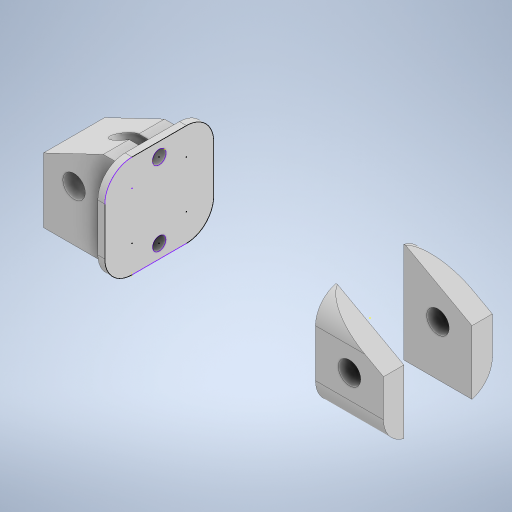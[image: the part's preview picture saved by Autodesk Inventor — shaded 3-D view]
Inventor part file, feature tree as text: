
AUTODESK INVENTOR PART (.ipt)
format: ipt  version: 2024 (Build 280153000, 153)  size: 498,176 bytes
history: native  units: mm
features: sketch x25, extrude x19, chamfer x3, plane x2, split x2, move_body x2, fillet x1, boolean_combine x1
ambient origin geometry x8: Origin, YZ Plane, XZ Plane, XY Plane, X Axis, Y Axis, Z Axis, Center Point
bodies: Solid1 (feature_tree), Solid2 (feature_tree), Solid3 (feature_tree), Solid4 (feature_tree), Solid5 (feature_tree)
feature tree (55):
  extrude  "Extrusion1"  Depth=16.0mm
  sketch  "Sketch2"  dims[d2=15.0mm d3=0.0mm d4=10.0mm]
  extrude  "Extrusion2"  Depth=10.0mm
  chamfer  "Chamfer1"  Distance=21.25mm
  extrude  "Extrusion3"  Depth=10.0mm TaperAngle=0.0deg
  extrude  "Extrusion4"  Depth=11.5mm TaperAngle=0.0deg
  extrude  "Extrusion5"  Depth=1.0mm TaperAngle=0.0deg
  chamfer  "Chamfer2"  Distance=6.0mm Angle=45.0deg
  sketch  "Sketch6"  dims[d14=7.0mm d15=11.5mm d16=0.0mm]
  extrude  "Extrusion6"  Depth=9.0mm
  extrude  "Extrusion7"  Depth=11.5mm TaperAngle=0.0deg
  chamfer  "Chamfer3"  Distance=11.5mm Angle=45.0deg
  sketch  "Sketch9"  dims[d26=3.3mm d27=45.25mm d28=0.0mm d29=11.5mm d30=5.5mm d31=45.0deg]
  extrude  "Extrusion8"  Depth=65.75mm TaperAngle=0.0deg
  extrude  "Extrusion9"  Depth=9.0mm TaperAngle=0.0deg
  extrude  "Extrusion10"  Depth=13.0mm TaperAngle=0.0deg
  sketch  "Sketch13"  dims[d43=24.0mm d44=21.0mm d45=0.0mm]
  extrude  "Extrusion11"  Depth=21.0mm TaperAngle=0.0deg
  extrude  "Extrusion12"  TaperAngle=0.0deg  [1 undecoded]
  extrude  "Extrusion13"  Depth=6.0mm TaperAngle=0.0deg
  plane  "Work Plane1"
  split  "Split1"
  move_body  "Move Body1"
  extrude  "Extrusion14"  Depth=0.5mm TaperAngle=0.0deg
  move_body  "Move Body2"
  fillet  "Fillet1"  Radius=10.0mm
  extrude  "Extrusion15"  Depth=10.0mm TaperAngle=0.0deg
  sketch  "Sketch19"  dims[d71=29.5mm d72=0.0mm d73=13.75mm]
  sketch  "Sketch20"
  extrude  "Extrusion16"  Depth=31.0mm
  extrude  "Extrusion18"  Depth=13.75mm
  extrude  "Extrusion19"  [1 undecoded]
  sketch  "Sketch23"
  sketch  "Sketch24"
  extrude  "Extrusion20"  [1 undecoded]
  plane  "Work Plane2"
  boolean_combine  "Combine1"
  split  "Split2"
  sketch  "Sketch26"
  sketch  "Sketch1"  dims[d0=36.0mm d1=16.0mm]
  sketch  "Sketch3"  dims[d5=10.0mm]
  sketch  "Sketch4"  dims[d6=3.3mm d7=21.25mm d8=0.0mm]
  sketch  "Sketch5"  dims[d9=10.0mm d10=5.5mm d11=45.0deg d12=10.0mm d13=0.0mm]
  sketch  "Sketch7"  dims[d17=3.3mm d18=1.0mm d19=0.0mm d20=6.0mm d21=11.5mm d22=45.0deg]
  sketch  "Sketch8"  dims[d23=15.0mm d24=0.0mm d25=9.0mm]
  sketch  "Sketch10"  dims[d32=2.0mm d33=65.75mm d34=0.0mm]
  sketch  "Sketch11"  dims[d35=0.5mm d36=0.0mm d37=9.0mm d38=0.0mm]
  sketch  "Sketch12"  dims[d39=0.5mm d40=0.0mm d41=13.0mm d42=0.0mm]
  sketch  "Sketch14"  dims[d46=12.25mm d47=-12.0mm d48=0.0mm d49=0.0mm]
  sketch  "Sketch15"  dims[d50=30.0mm d51=0.0mm d52=6.0mm d53=0.0mm d54=0.0mm d55=4.0mm]
  sketch  "Sketch16"  dims[d56=0.5mm d57=0.0mm d58=0.5mm d59=0.0mm d64=10.0mm d65=0.0mm]
  sketch  "Sketch17"  dims[d66=3.0mm d67=10.0mm d68=0.0mm]
  sketch  "Sketch18"  dims[d69=1.0mm d70=31.0mm]
  sketch  "Sketch22"
  sketch  "Sketch25"
note: 3 required parameter values undecoded (feature->parameter linkage not recoverable at this tier; creation-order binding heuristic only, values carry confidence <= 0.55)
